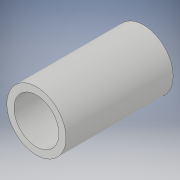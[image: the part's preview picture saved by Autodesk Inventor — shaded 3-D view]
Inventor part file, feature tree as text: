
AUTODESK INVENTOR PART (.ipt)
format: ipt  version: 2019 (Build 230136000, 136)  size: 96,768 bytes
history: native  units: in
note: dims shown in document units (in); Inventor stores cm internally (conversion verified against a paired STEP export)
features: extrude x1, sketch x1
ambient origin geometry x8: Origin, YZ Plane, XZ Plane, XY Plane, X Axis, Y Axis, Z Axis, Center Point
bodies: Solid1 (feature_tree)
feature tree (2):
  extrude  "Extrusion1"  Depth=3.015in
  sketch  "Sketch1"  dims[d0=1.265in d1=0.2in d2=3.015in d3=0.0in]
